# Revit family: 0005170
name_source: partatom
category: Lighting Fixtures
revit_build: Autodesk Revit 2017 (Build: 20190507_1515(x64)
units: mm (PartAtom-declared; Revit-internal decimal feet)

## family parameters
Cut with Voids When Loaded = No
Host = Face
Light Source = No
OmniClass Number = 23.80.70.00
OmniClass Title = Lighting
Part Type = Normal
Room Calculation Point = No
Round Connector Dimension = Use Diameter
Shared = No

## types (2) — shared parameters
Apparent Load = 9 VA
Assembly Code = D5020200
AssetType = Fixed
ClassificationName = Uniclass2015
ClassificationValue = EF_70_80
Default Elevation = 1219 mm
Description = Integrated LED recessed spotlight, vertical tilt 30°, white bezel colour, white repleceable reflector, 740lm, 9.0W, dimmable trailing/leading edge, 3000K, 40° degree beam angle, polycarbonate and aluminium body, low profile 62mm recessed depth, IP44 from the front, IK03, loop-in/loop-out terminals for fast wiring, weight 0,165Kg, 85mm bezel diameter, 68-74mm cutout, clear lens. Additional black reflector included in the packaging. Lifetime: 30.000 hours at L70. Energy Class: A++, A+, A.
DocumentationLiterature = http://www.sylvania-lighting.com
ElectricShockClassification = Class II
IfcExportAs = IfcLightFixtureType
IfcExportType = IfcLightFixtureType
ImpactProtectionIndex = IK03
IngressProtection = IP20/IP44
InputNominalFrequency = 50/60 Hz
InputVoltage = 220-240 V AC
Keynote = 16500
Lamp = LED
LampColourRenderingIndex = 80
LampColourTemperature = 3000 K
LampsType = LED
Manufacturer = Feilo Sylvania
ManufacturerName = Feilo Sylvania
Material_1_SYL = ABS Plastic
Material_2_SYL = Brushed Aluminum
ModelNumber = 0005170
NominalDepth = 86 mm  [stored 0.282152 ft]
NominalHeight = 64 mm  [stored 0.209974 ft]
NominalLength = 86 mm  [stored 0.282152 ft]
PowerConsumption = 9 W
Type Image = <None>
URL = http://www.sylvania-lighting.com
Voltage = 230 V
zero-valued in all types: Cost, PowerFactor

## per-type parameters (varying)
| type | LampNominalLuminous | LuminousEfficacy | Model | ModelReference | Name | TypeLamp_SYL | TypeName |
| 0005170 START ECO SPOT ALU 740LM 830 IP44 WHT + WHT Refl | 740 lm | 82.22 lm/W | Start eco Spot Aluminium 740lm 830 IP44 WHT + WHT Refl | Start eco Spot Aluminium 740lm 830 IP44 WHT + WHT Refl | Start eco Spot Aluminium 740lm 830 IP44 WHT + WHT Refl | START eco Spot Aluminium lamp : 0005170 START ECO SPOT ALU 740LM 830 IP44 WHT + WHT Refl | Start eco Spot Aluminium 740lm 830 IP44 WHT + WHT Refl |
| 0005170 START ECO SPOT ALU 740LM 830 IP44 WHT + BLK Refl | 660 lm | 73.33 lm/W | Start eco Spot Aluminium 660lm 830 IP44 WHT + BLK Refl | Start eco Spot Aluminium 660lm 830 IP44 WHT + BLK Refl | Start eco Spot Aluminium 660lm 830 IP44 WHT + BLK Refl | START eco Spot Aluminium lamp : 0005170 START ECO SPOT ALU 740LM 830 IP44 WHT + BLK Refl | Start eco Spot Aluminium 660lm 830 IP44 WHT + BLK Refl |

note: [stored X ft] marks values corroborated as IEEE doubles in the binary element streams (Revit-internal decimal feet)

## geometry (parser evidence)
native form markers: Sweep x4
no freeform markers — native parametric forms only
